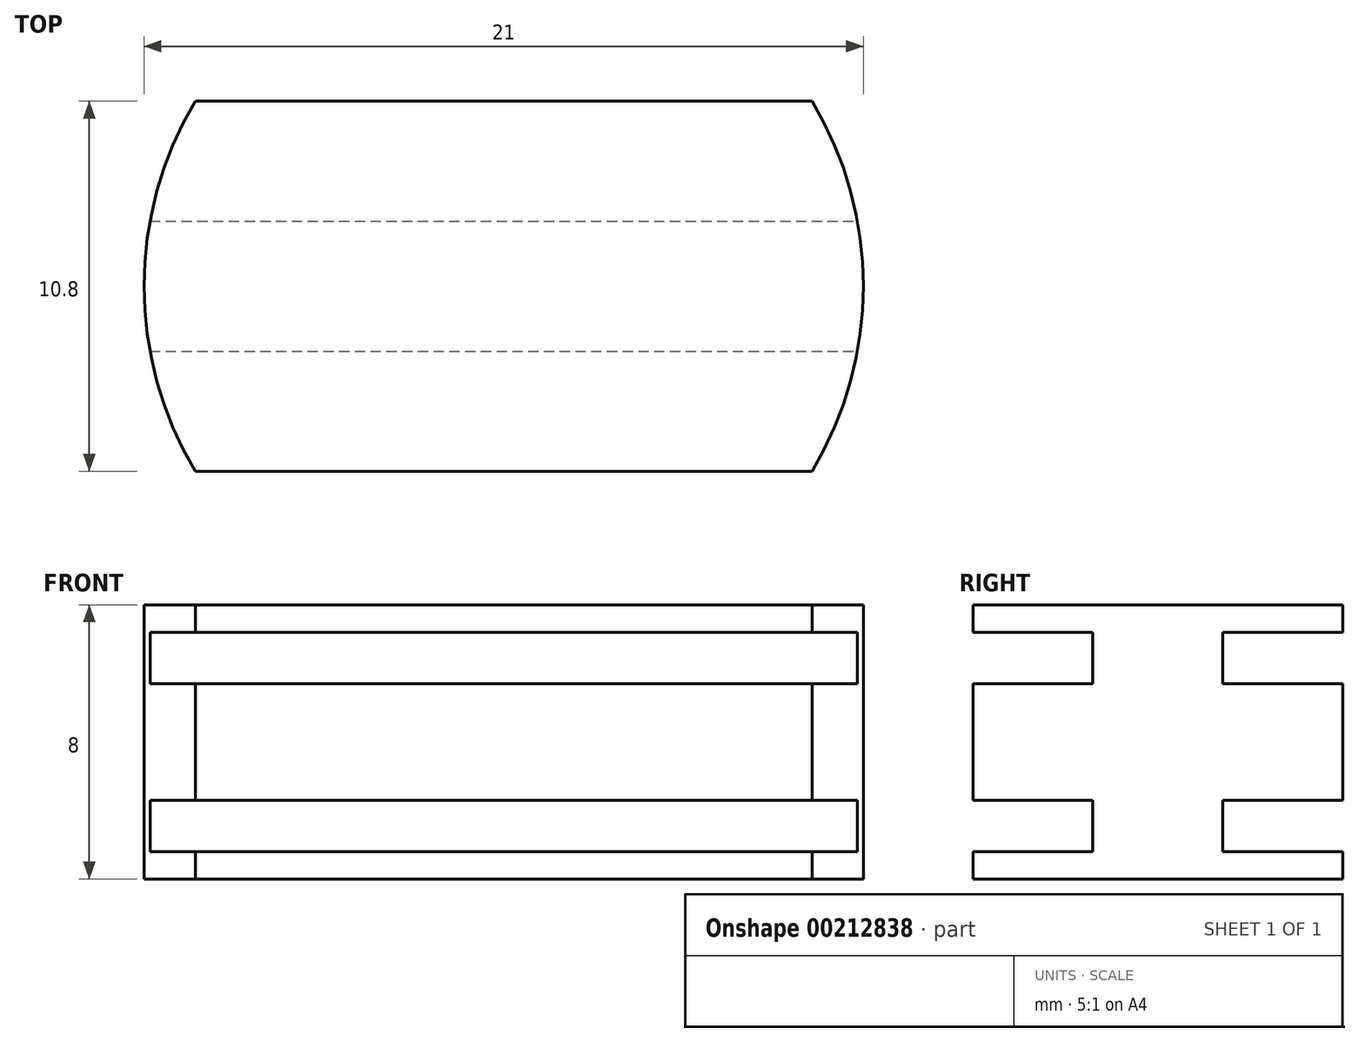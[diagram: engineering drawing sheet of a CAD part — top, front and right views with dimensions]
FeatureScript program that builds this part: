
annotation { "Feature Type Name" : "Feature", "Feature Type Description" : "" }
export const myFeature = defineFeature(function(context is Context, id is Id, definition is map)
    precondition{}
    {
        {
            var Q0;
            Q0=qCreatedBy(makeId("Top.planeOp"),FACE);
            var sketch = newSketch(context, id + "F0", { "sketchPlane" : qUnion([Q0])});
            skLineSegment(sketch, "E0.bottom", {"start": v(9, 5.4) * mm, "end": v(-9, 5.4) * mm});
            skLineSegment(sketch, "E0.top", {"start": v(9, -5.4) * mm, "end": v(-9, -5.4) * mm});
            skPoint(sketch, "E0.middle", {"position": v(0, 0) * mm});
            skArc(sketch, "E1", {"start": v(-9, 5.4) * mm, "mid": v(-10.5, 0) * mm, "end": v(-9, -5.4) * mm});
            skArc(sketch, "E2.trimOffspring", {"start": v(9, -5.4) * mm, "mid": v(10.5, 0) * mm, "end": v(9, 5.4) * mm});
            skSolve(sketch);
        }
        {
            var Q0;
            Q0=makeQuery(id+"F0.imprint","IMPRINT",FACE,{"disambiguationData":[TD([[makeQuery(id+"F0.imprint","IMPRINT",EDGE,{"derivedFrom":sQuery(id+"F0.wireOp",EDGE,"E0.bottom")}),1.0]])]});
            extrude(context, id + "F1", {"entities" : qUnion([Q0]), "oppositeDirection" : true, "depth" : 8 * mm});
        }
        {
            var Q0;
            Q0=qCreatedBy(makeId("Right.planeOp"),FACE);
            var sketch = newSketch(context, id + "F2", { "sketchPlane" : qUnion([Q0])});
            skLineSegment(sketch, "E3.0.1", {"start": v(5.4, -0.8) * mm, "end": v(5.4, -2.3) * mm});
            skLineSegment(sketch, "E3.0.3", {"start": v(-5.4, -2.3) * mm, "end": v(-5.4, -0.8) * mm});
            skLineSegment(sketch, "E4.bottom", {"start": v(5.4, -0.8) * mm, "end": v(1.9, -0.8) * mm});
            skLineSegment(sketch, "E4.top", {"start": v(5.4, -2.3) * mm, "end": v(1.9, -2.3) * mm});
            skLineSegment(sketch, "E4.right", {"start": v(1.9, -0.8) * mm, "end": v(1.9, -2.3) * mm});
            skLineSegment(sketch, "E5.MirrorCS", {"start": v(-5.4, -0.8) * mm, "end": v(-1.9, -0.8) * mm});
            skLineSegment(sketch, "E6.MirrorCS", {"start": v(-1.9, -0.8) * mm, "end": v(-1.9, -2.3) * mm});
            skLineSegment(sketch, "E7.MirrorCS", {"start": v(-5.4, -2.3) * mm, "end": v(-1.9, -2.3) * mm});
            skPoint(sketch, "E8.orphan", {"position": v(5.4, 0) * mm});
            skPoint(sketch, "E9.orphan", {"position": v(-5.4, 0) * mm});
            skPoint(sketch, "E10.MirrorCS.end.orphan", {"position": v(-5.4, -2.3) * mm});
            skPoint(sketch, "E10.MirrorCS.start.orphan", {"position": v(-5.4, -0.8) * mm});
            skPoint(sketch, "E3.0.2.end.orphan", {"position": v(-5.4, -8) * mm});
            skPoint(sketch, "E3.0.2.start.orphan", {"position": v(5.4, -8) * mm});
            skLineSegment(sketch, "E11", {"start": v(13.48, -4) * mm, "end": v(-14.73, -4) * mm, "construction": true});
            skLineSegment(sketch, "E12.MirrorCS", {"start": v(-5.4, -5.7) * mm, "end": v(-5.4, -7.2) * mm});
            skLineSegment(sketch, "E13.MirrorCS", {"start": v(-5.4, -7.2) * mm, "end": v(-1.9, -7.2) * mm});
            skLineSegment(sketch, "E14.MirrorCS", {"start": v(-5.4, -5.7) * mm, "end": v(-1.9, -5.7) * mm});
            skLineSegment(sketch, "E15.MirrorCS", {"start": v(-1.9, -7.2) * mm, "end": v(-1.9, -5.7) * mm});
            skLineSegment(sketch, "E16.MirrorCS", {"start": v(5.4, -7.2) * mm, "end": v(5.4, -5.7) * mm});
            skLineSegment(sketch, "E17.MirrorCS", {"start": v(5.4, -5.7) * mm, "end": v(1.9, -5.7) * mm});
            skLineSegment(sketch, "E18.MirrorCS", {"start": v(5.4, -7.2) * mm, "end": v(1.9, -7.2) * mm});
            skLineSegment(sketch, "E19.MirrorCS", {"start": v(1.9, -7.2) * mm, "end": v(1.9, -5.7) * mm});
            skSolve(sketch);
        }
        {
            var Q0;
            Q0 = qSketchRegion(id + "F2", true);
            extrude(context, id + "F3", {"entities" : qUnion([Q0]), "operationType" : NewBodyOperationType.REMOVE, "endBound" : BoundingType.SYMMETRIC, "oppositeDirection" : true, "depth" : 25 * mm});
        }
    });
